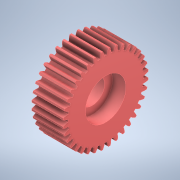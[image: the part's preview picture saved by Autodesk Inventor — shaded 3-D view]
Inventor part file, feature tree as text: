
AUTODESK INVENTOR PART (.ipt)
format: ipt  version: 2022 (Build 260153000, 153)  size: 315,904 bytes
history: mixed  units: in
note: dims shown in document units (in); Inventor stores cm internally (conversion verified against a paired STEP export)
features: extrude x1, sketch x1, other x1, imported_body x1
ambient origin geometry x8: Origin, YZ Plane, XZ Plane, XY Plane, X Axis, Y Axis, Z Axis, Center Point
bodies: Solid1 (imported_parasolid)
feature tree (4):
  extrude  "Extrusion1"  [1 undecoded]
  sketch  "Sketch2"  dims[d0=0.1181in d1=0.0in]
  other  "36_Teeth_Planet_Gear.STEP"
  imported_body  NMx_Import_Brep_tag  [imported B-rep: ~149 faces, bbox_mm=[7.0, 18.957585, 18.957585]]
note: 1 required parameter value undecoded (feature->parameter linkage not recoverable at this tier; creation-order binding heuristic only, values carry confidence <= 0.55)
